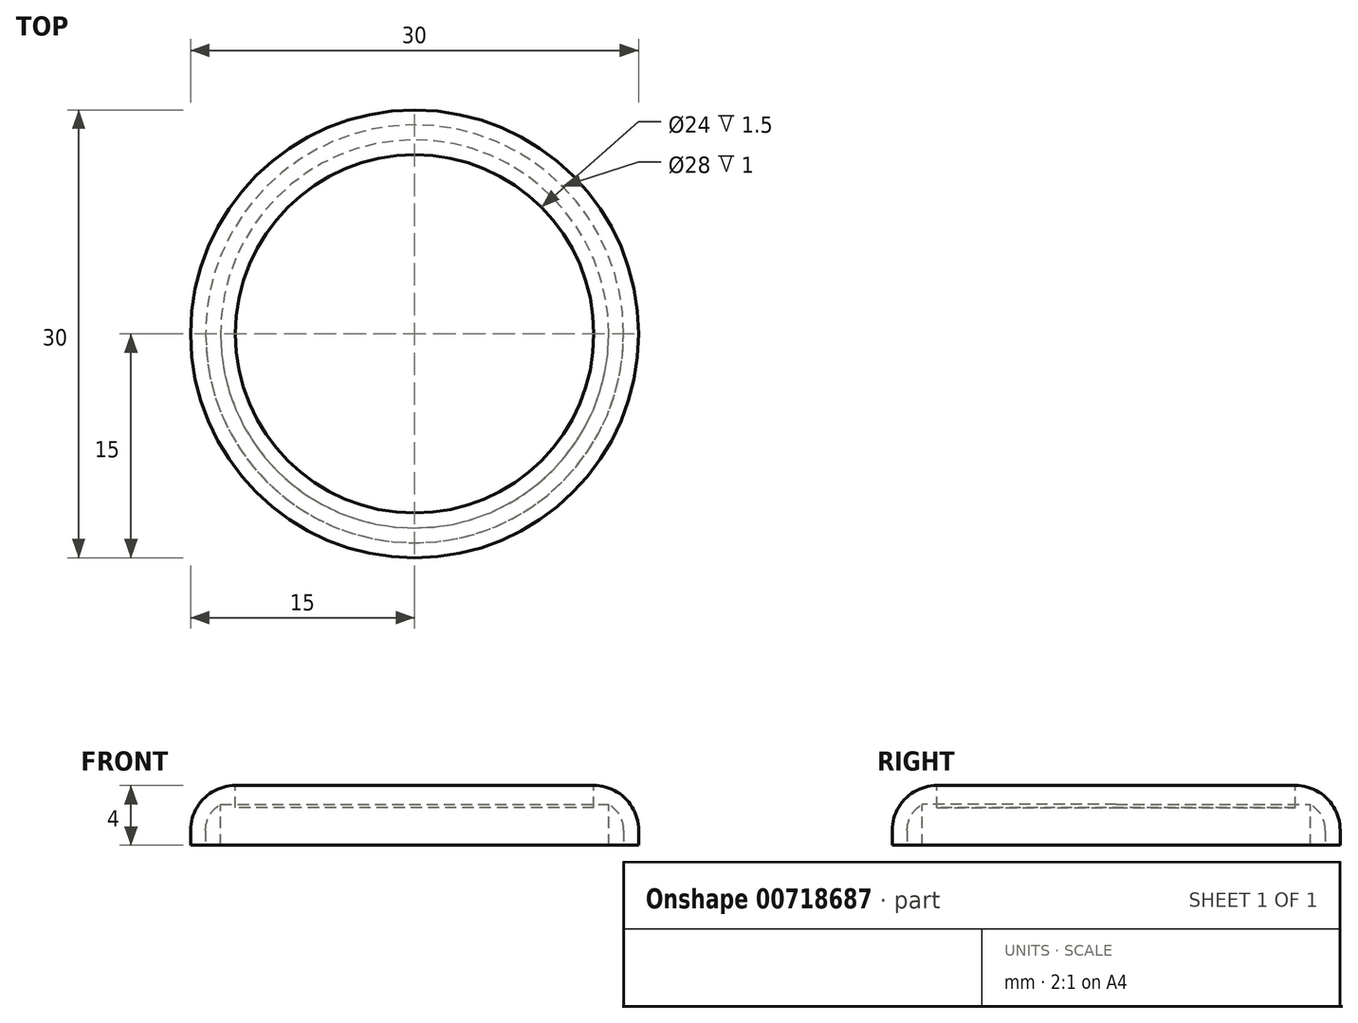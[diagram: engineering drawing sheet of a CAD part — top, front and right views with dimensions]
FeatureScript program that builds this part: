
annotation { "Feature Type Name" : "Feature", "Feature Type Description" : "" }
export const myFeature = defineFeature(function(context is Context, id is Id, definition is map)
    precondition{}
    {
        {
            var Q0;
            Q0=qCreatedBy(makeId("Top.planeOp"),FACE);
            var sketch = newSketch(context, id + "F0", { "sketchPlane" : qUnion([Q0])});
            skCircle(sketch, "E0", {"center": v(0, 0) * mm, "radius": 15 * mm});
            skSolve(sketch);
        }
        {
            var Q0;
            Q0 = qSketchRegion(id + "F0", true);
            extrude(context, id + "F1", {"entities" : qUnion([Q0]), "depth" : 4 * mm, "offsetDistance" : 25.4 * mm});
        }
        {
            var Q0;
            Q0=makeQuery(id+"F1.opExtrude","CAP_EDGE",EDGE,{"disambiguationData":[OSD([sQuery(id+"F0.wireOp",EDGE,"E0")])],"isStart":false});
            fillet(context, id + "F2", {"entities" : qUnion([Q0]), "radius" : 3 * mm, "tangentPropagation" : true, "allowEdgeOverflow" : false});
        }
        {
            var Q0;
            Q0=makeQuery(id+"F1.opExtrude","CAP_FACE",FACE,{"disambiguationData":[OSD([sQuery(id+"F0.wireOp",EDGE,"E0")])],"isStart":false});
            extrude(context, id + "F3", {"entities" : qUnion([Q0]), "operationType" : NewBodyOperationType.REMOVE, "oppositeDirection" : true, "depth" : 1.5 * mm, "offsetDistance" : 25.4 * mm});
        }
        {
            var Q0;
            Q0=makeQuery(id+"F1.opExtrude","CAP_FACE",FACE,{"disambiguationData":[OSD([sQuery(id+"F0.wireOp",EDGE,"E0")])],"isStart":true});
            shell(context, id + "F4", {"entities" : qUnion([Q0]), "thickness" : 1 * mm});
        }
        {
            var Q0;
            {var subQ0=sQuery(id+"F0.wireOp",EDGE,"E0");Q0=makeQuery(id+"F4.opShell","OFFSET_FACE",FACE,{"disambiguationData":[OSD([subQ0]),TDD([makeQuery(id+"F3.boolean.opBoolean","COPY",FACE,{"derivedFrom":makeQuery(id+"F3.opExtrude","CAP_FACE",FACE,{"disambiguationData":[OSD([subQ0])],"isStart":false})})])]});}
            extrude(context, id + "F5", {"entities" : qUnion([Q0]), "operationType" : NewBodyOperationType.ADD, "depth" : 1.5 * mm, "offsetDistance" : 25.4 * mm});
        }
    });
